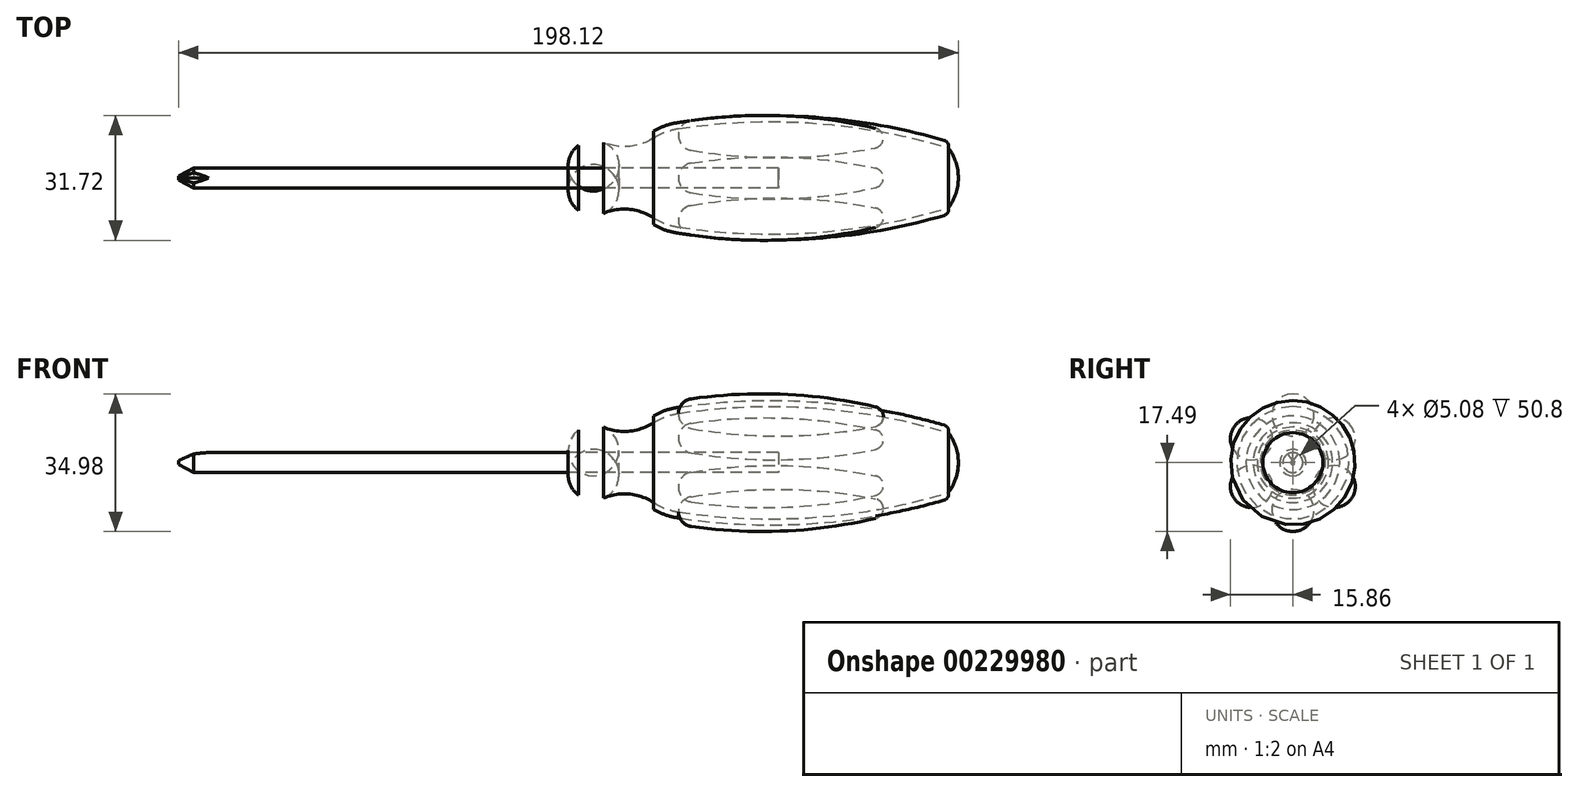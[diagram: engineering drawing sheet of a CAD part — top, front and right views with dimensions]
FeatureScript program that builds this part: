
annotation { "Feature Type Name" : "Feature", "Feature Type Description" : "" }
export const myFeature = defineFeature(function(context is Context, id is Id, definition is map)
    precondition{}
    {
        {
            var Q0;
            Q0=qCreatedBy(makeId("Front.planeOp"),FACE);
            var sketch = newSketch(context, id + "F0", { "sketchPlane" : qUnion([Q0])});
            skLineSegment(sketch, "E0", {"start": v(-101.6, 0) * mm, "end": v(96.52, 0) * mm});
            skLineSegment(sketch, "E1", {"start": v(96.52, 0) * mm, "end": v(117.55, 0) * mm, "construction": true});
            skLineSegment(sketch, "E2", {"start": v(50.8, 2.54) * mm, "end": v(-97.8, 2.54) * mm});
            skLineSegment(sketch, "E3", {"start": v(-101.6, 0.5) * mm, "end": v(-101.6, 0) * mm});
            skLineSegment(sketch, "E4", {"start": v(0, 2.54) * mm, "end": v(0, 8.25) * mm});
            skArc(sketch, "E5", {"start": v(6.35, 9.02) * mm, "mid": v(3.07, 9.48) * mm, "end": v(0, 8.25) * mm});
            skArc(sketch, "E6", {"start": v(6.35, 9.02) * mm, "mid": v(12.84, 7.99) * mm, "end": v(19.05, 10.11) * mm});
            skArc(sketch, "E7", {"start": v(25.4, 12.52) * mm, "mid": v(22.1, 11.65) * mm, "end": v(19.05, 10.11) * mm});
            skArc(sketch, "E8", {"start": v(93.98, 7.62) * mm, "mid": v(59.96, 13.9) * mm, "end": v(25.4, 12.52) * mm});
            skArc(sketch, "E9", {"start": v(96.52, 0) * mm, "mid": v(95.87, 4.02) * mm, "end": v(93.98, 7.62) * mm});
            skArc(sketch, "E10.0", {"start": v(25.17, 14.02) * mm, "mid": v(22.01, 13.24) * mm, "end": v(19.05, 11.9) * mm});
            skArc(sketch, "E10.1", {"start": v(92.95, 9.52) * mm, "mid": v(59.3, 15.46) * mm, "end": v(25.17, 14.02) * mm});
            skLineSegment(sketch, "E11", {"start": v(19.05, 11.9) * mm, "end": v(19.05, 10.11) * mm});
            skArc(sketch, "E12", {"start": v(93.98, 7.62) * mm, "mid": v(93.86, 8.78) * mm, "end": v(92.95, 9.52) * mm});
            skPoint(sketch, "E13.orphan", {"position": v(0, 0) * mm});
            skLineSegment(sketch, "E14", {"start": v(50.8, 2.54) * mm, "end": v(50.8, 0) * mm});
            skLineSegment(sketch, "E15", {"start": v(-101.6, 0.5) * mm, "end": v(-97.8, 2.54) * mm});
            skPoint(sketch, "E16.orphan", {"position": v(-101.6, 2.54) * mm});
            skSolve(sketch);
        }
        {
            var Q0;
            Q0=qCreatedBy(makeId("Front.planeOp"),FACE);
            var sketch = newSketch(context, id + "F1", { "sketchPlane" : qUnion([Q0])});
            skLineSegment(sketch, "E17", {"start": v(25.4, 12.52) * mm, "end": v(77.47, 11.64) * mm});
            skArc(sketch, "E18", {"start": v(28.67, 16.22) * mm, "mid": v(26.35, 14.97) * mm, "end": v(25.4, 12.52) * mm});
            skArc(sketch, "E19", {"start": v(77.47, 11.64) * mm, "mid": v(76.93, 13.25) * mm, "end": v(75.5, 14.16) * mm});
            skArc(sketch, "E20", {"start": v(75.5, 14.16) * mm, "mid": v(52.19, 17.37) * mm, "end": v(28.67, 16.22) * mm});
            skSolve(sketch);
        }
        {
            var Q0;
            Q0=qCreatedBy(makeId("Front.planeOp"),FACE);
            var sketch = newSketch(context, id + "F2", { "sketchPlane" : qUnion([Q0])});
            skLineSegment(sketch, "E21", {"start": v(-101.6, 0.5) * mm, "end": v(-93.98, 2.54) * mm});
            skSolve(sketch);
        }
        {
            var Q0;
            Q0=sQuery(id+"F2.wireOp",VERTEX,"E21.start");
            var Q1;
            Q1=sQuery(id+"F2.wireOp",EDGE,"E21");
            cPlane(context, id + "F3", {"entities" : qUnion([Q0, Q1]), "cplaneType" : CPlaneType.LINE_POINT, "offset" : 25.4 * mm, "width" : 152.4 * mm, "height" : 152.4 * mm});
        }
        {
            var Q0;
            Q0=qCreatedBy(id+"F3.planeOp",FACE);
            var sketch = newSketch(context, id + "F4", { "sketchPlane" : qUnion([Q0])});
            skLineSegment(sketch, "E22", {"start": v(5.08, 29.2) * mm, "end": v(0, 26.67) * mm});
            skLineSegment(sketch, "E23", {"start": v(0, 26.67) * mm, "end": v(-5.08, 29.2) * mm});
            skLineSegment(sketch, "E24", {"start": v(-5.08, 29.2) * mm, "end": v(5.08, 29.2) * mm});
            skLineSegment(sketch, "E25", {"start": v(0, 29.2) * mm, "end": v(0, 26.67) * mm, "construction": true});
            skSolve(sketch);
        }
        {
            var Q0;
            {var subQ0=sQuery(id+"F0.wireOp",EDGE,"E3");Q0=makeQuery(id+"F0.imprint","IMPRINT",FACE,{"disambiguationData":[TD([[makeQuery(id+"F0.imprint","IMPRINT",EDGE,{"derivedFrom":subQ0}),1.0]])]});}
            var Q1;
            Q1=sQuery(id+"F0.wireOp",EDGE,"E1");
            revolve(context, id + "F5", {"entities" : qUnion([Q0]), "axis" : qUnion([Q1]), "revolveType" : RevolveType.FULL});
        }
        {
            var Q0;
            {var subQ0=sQuery(id+"F0.wireOp",EDGE,"E4");Q0=makeQuery(id+"F0.imprint","IMPRINT",FACE,{"disambiguationData":[TD([[makeQuery(id+"F0.imprint","IMPRINT",EDGE,{"derivedFrom":subQ0}),-1.0]])]});}
            var Q1;
            Q1=sQuery(id+"F0.wireOp",EDGE,"E1");
            revolve(context, id + "F6", {"entities" : qUnion([Q0]), "axis" : qUnion([Q1]), "revolveType" : RevolveType.FULL});
        }
        {
            var Q0;
            Q0=makeQuery(id+"F0.imprint","IMPRINT",FACE,{"disambiguationData":[TD([[makeQuery(id+"F0.imprint","IMPRINT",EDGE,{"derivedFrom":sQuery(id+"F0.wireOp",EDGE,"E7")}),-1.0]])]});
            var Q1;
            Q1=sQuery(id+"F0.wireOp",EDGE,"E1");
            revolve(context, id + "F7", {"entities" : qUnion([Q0]), "axis" : qUnion([Q1]), "revolveType" : RevolveType.FULL});
        }
        {
            var Q0;
            Q0=makeQuery(id+"F1.imprint","IMPRINT",FACE,{"disambiguationData":[TD([[makeQuery(id+"F1.imprint","IMPRINT",EDGE,{"derivedFrom":sQuery(id+"F1.wireOp",EDGE,"E17")}),1.0]])]});
            var Q1;
            Q1=sQuery(id+"F1.wireOp",EDGE,"E17");
            revolve(context, id + "F8", {"entities" : qUnion([Q0]), "axis" : qUnion([Q1]), "revolveType" : RevolveType.FULL});
        }
        {
            var Q0;
            Q0=makeQuery(id+"F8.opRevolve","SWEPT_BODY",BODY,{"disambiguationData":[OSD([sQuery(id+"F1.wireOp",EDGE,"E17"),sQuery(id+"F1.wireOp",EDGE,"E18"),sQuery(id+"F1.wireOp",EDGE,"E19"),sQuery(id+"F1.wireOp",EDGE,"E20")])]});
            var Q1;
            Q1=sQuery(id+"F0.wireOp",EDGE,"E1");
            circularPattern(context, id + "F9", {"entities" : qUnion([Q0]), "axis" : qUnion([Q1]), "angle" : 360 * degree, "instanceCount" : 6, "equalSpace" : true});
        }
        {
            var Q0;
            Q0=makeQuery(id+"F6.opRevolve","SWEPT_BODY",BODY,{"disambiguationData":[OSD([sQuery(id+"F0.wireOp",EDGE,"E0"),sQuery(id+"F0.wireOp",EDGE,"E2"),sQuery(id+"F0.wireOp",EDGE,"E4"),sQuery(id+"F0.wireOp",EDGE,"E5"),sQuery(id+"F0.wireOp",EDGE,"E6"),sQuery(id+"F0.wireOp",EDGE,"E7"),sQuery(id+"F0.wireOp",EDGE,"E8"),sQuery(id+"F0.wireOp",EDGE,"E9"),sQuery(id+"F0.wireOp",EDGE,"E14")])]});
            var Q1;
            Q1=makeQuery(id+"F5.opRevolve","SWEPT_BODY",BODY,{"disambiguationData":[OSD([sQuery(id+"F0.wireOp",EDGE,"E0"),sQuery(id+"F0.wireOp",EDGE,"E2"),sQuery(id+"F0.wireOp",EDGE,"E3"),sQuery(id+"F0.wireOp",EDGE,"E14"),sQuery(id+"F0.wireOp",EDGE,"E15")])]});
            var Q2;
            Q2=makeQuery(id+"F7.opRevolve","SWEPT_BODY",BODY,{"disambiguationData":[OSD([sQuery(id+"F0.wireOp",EDGE,"E7"),sQuery(id+"F0.wireOp",EDGE,"E8"),sQuery(id+"F0.wireOp",EDGE,"E10.0"),sQuery(id+"F0.wireOp",EDGE,"E10.1"),sQuery(id+"F0.wireOp",EDGE,"E11"),sQuery(id+"F0.wireOp",EDGE,"E12")])]});
            booleanBodies(context, id + "F10", {"operationType" : BooleanOperationType.SUBTRACTION, "tools" : qUnion([Q0, Q1]), "targets" : qUnion([Q2]), "keepTools" : true});
        }
        {
            var Q0;
            Q0=qSketchRegion(id+"F4",true);
            var Q1;
            Q1=qConstructionFilter(qBodyType(qCreatedBy(id+"F2",EDGE),BodyType.WIRE),ConstructionObject.NO);
            sweep(context, id + "F11", {"operationType" : NewBodyOperationType.REMOVE, "profiles" : qUnion([Q0]), "path" : qUnion([Q1])});
        }
    });
